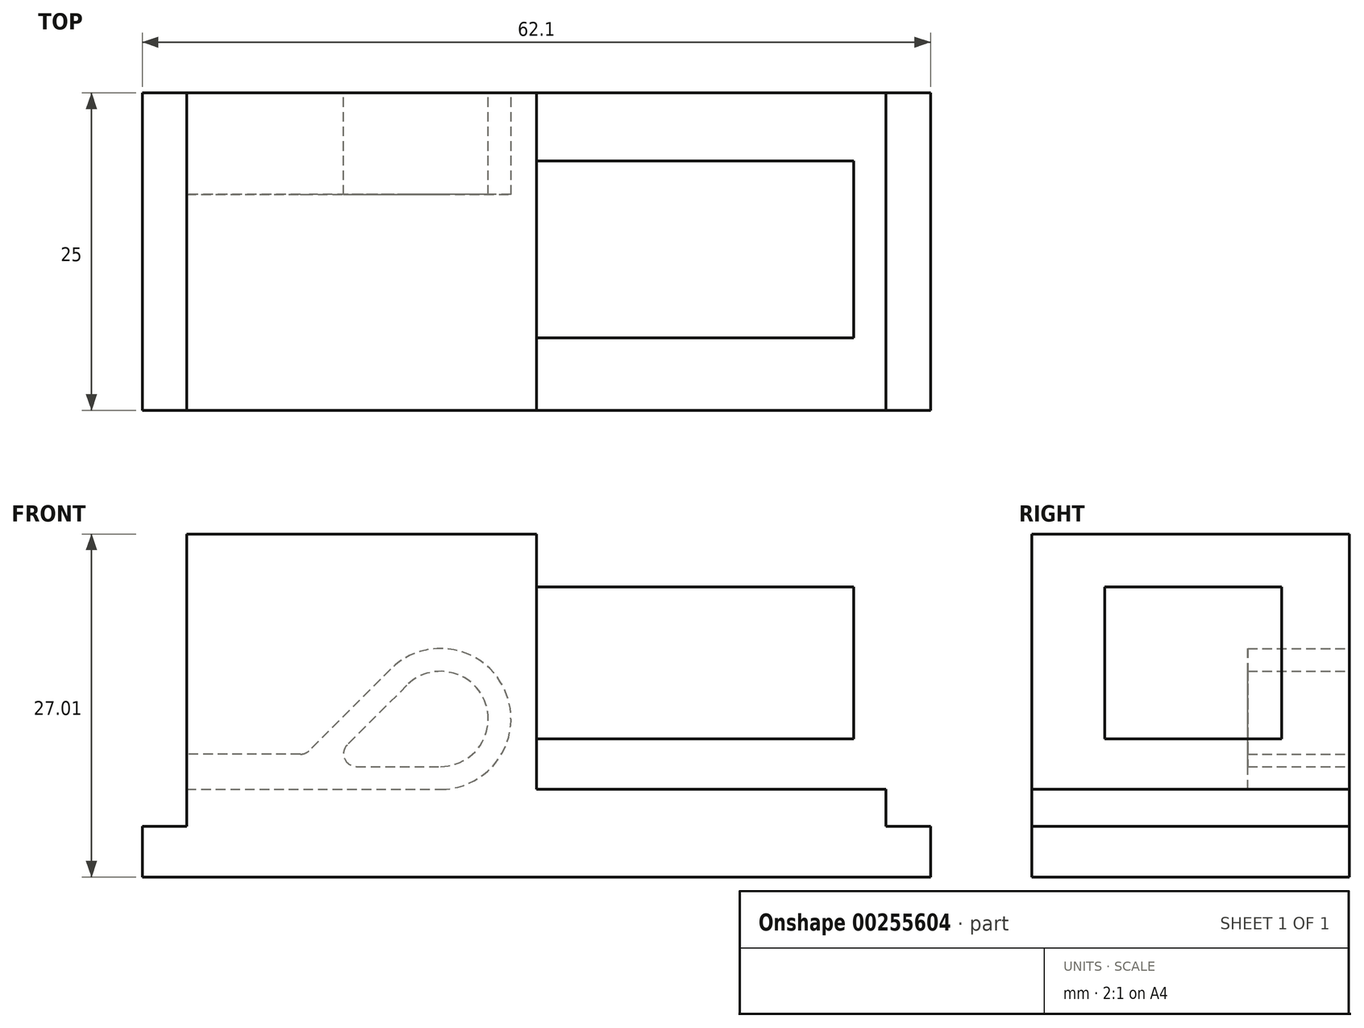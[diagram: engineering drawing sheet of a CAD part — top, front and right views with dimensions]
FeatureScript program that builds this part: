
annotation { "Feature Type Name" : "Feature", "Feature Type Description" : "" }
export const myFeature = defineFeature(function(context is Context, id is Id, definition is map)
    precondition{}
    {
        {
            var Q0;
            Q0=qCreatedBy(makeId("Front.planeOp"),FACE);
            var sketch = newSketch(context, id + "F0", { "sketchPlane" : qUnion([Q0])});
            skLineSegment(sketch, "E0.bottom", {"start": v(-31.05, 0) * mm, "end": v(31.05, 0) * mm});
            skLineSegment(sketch, "E0.top", {"start": v(-31.05, 4) * mm, "end": v(-27.55, 4) * mm});
            skLineSegment(sketch, "E0.left", {"start": v(-31.05, 0) * mm, "end": v(-31.05, 4) * mm});
            skLineSegment(sketch, "E0.right", {"start": v(31.05, 0) * mm, "end": v(31.05, 4) * mm});
            skLineSegment(sketch, "E1", {"start": v(-27.55, 4) * mm, "end": v(-27.55, 27.01) * mm});
            skLineSegment(sketch, "E2", {"start": v(-27.55, 6.9) * mm, "end": v(-7.55, 6.9) * mm});
            skLineSegment(sketch, "E3", {"start": v(27.55, 6.9) * mm, "end": v(27.55, 4) * mm});
            skLineSegment(sketch, "E4.trimOffspring", {"start": v(27.55, 4) * mm, "end": v(31.05, 4) * mm});
            skLineSegment(sketch, "E5", {"start": v(-29.3, 9.9) * mm, "end": v(-29.3, -4.78) * mm, "construction": true});
            skLineSegment(sketch, "E6", {"start": v(29.3, -4.78) * mm, "end": v(29.3, 11.42) * mm, "construction": true});
            skLineSegment(sketch, "E7.bottom", {"start": v(-27.55, 27.01) * mm, "end": v(0, 27.01) * mm});
            skLineSegment(sketch, "E7.right", {"start": v(0, 27.01) * mm, "end": v(0, 6.9) * mm});
            skLineSegment(sketch, "E8", {"start": v(-14.19, 8.7) * mm, "end": v(-7.55, 8.7) * mm});
            skArc(sketch, "E9", {"start": v(-7.55, 8.7) * mm, "mid": v(-4.09, 13.89) * mm, "end": v(-10.2, 15.1) * mm});
            skLineSegment(sketch, "E10", {"start": v(-10.2, 15.1) * mm, "end": v(-14.9, 10.4) * mm});
            skArc(sketch, "E11", {"start": v(-7.55, 6.9) * mm, "mid": v(-2.42, 14.57) * mm, "end": v(-11.47, 16.37) * mm});
            skLineSegment(sketch, "E12", {"start": v(-11.47, 16.37) * mm, "end": v(-17.89, 9.96) * mm});
            skArc(sketch, "E13.filletArc", {"start": v(-14.9, 10.4) * mm, "mid": v(-15.11, 9.32) * mm, "end": v(-14.19, 8.7) * mm});
            skLineSegment(sketch, "E14", {"start": v(-18.6, 9.67) * mm, "end": v(-27.55, 9.67) * mm});
            skPoint(sketch, "E15.visualSharp", {"position": v(-18.18, 9.67) * mm});
            skArc(sketch, "E15.filletArc", {"start": v(-18.6, 9.67) * mm, "mid": v(-18.21, 9.75) * mm, "end": v(-17.89, 9.96) * mm});
            skPoint(sketch, "E16.orphan", {"position": v(0, 3.93) * mm});
            skLineSegment(sketch, "E17.trimOffspring", {"start": v(0, 6.9) * mm, "end": v(27.55, 6.9) * mm});
            skSolve(sketch);
        }
        {
            var Q0;
            Q0=makeQuery(id+"F0.imprint","IMPRINT",FACE,{"disambiguationData":[TD([[makeQuery(id+"F0.imprint","IMPRINT",EDGE,{"derivedFrom":sQuery(id+"F0.wireOp",EDGE,"E0.bottom")}),1.0]])]});
            var Q1;
            {var subQ0=sQuery(id+"F0.wireOp",EDGE,"E2");Q1=makeQuery(id+"F0.imprint","IMPRINT",FACE,{"disambiguationData":[TD([[makeQuery(id+"F0.imprint","IMPRINT",EDGE,{"derivedFrom":subQ0}),1.0]])]});}
            var Q2;
            Q2=makeQuery(id+"F0.imprint","IMPRINT",FACE,{"disambiguationData":[TD([[makeQuery(id+"F0.imprint","IMPRINT",EDGE,{"derivedFrom":sQuery(id+"F0.wireOp",EDGE,"E8")}),1.0]])]});
            extrude(context, id + "F1", {"entities" : qUnion([Q0, Q1, Q2]), "depth" : 25 * mm});
        }
        {
            var Q0;
            {var subQ0=sQuery(id+"F0.wireOp",EDGE,"E2");Q0=makeQuery(id+"F0.imprint","IMPRINT",FACE,{"disambiguationData":[TD([[makeQuery(id+"F0.imprint","IMPRINT",EDGE,{"derivedFrom":subQ0}),1.0]])]});}
            extrude(context, id + "F2", {"entities" : qUnion([Q0]), "operationType" : NewBodyOperationType.REMOVE, "depth" : 8 * mm});
        }
        {
            var Q0;
            Q0=makeQuery(id+"F1.opExtrude","SWEPT_FACE",FACE,{"disambiguationData":[OSD([sQuery(id+"F0.wireOp",EDGE,"E7.right")])]});
            var sketch = newSketch(context, id + "F3", { "sketchPlane" : qUnion([Q0])});
            skLineSegment(sketch, "E18.bottom", {"start": v(-19.28, 22.83) * mm, "end": v(-5.34, 22.83) * mm});
            skLineSegment(sketch, "E18.top", {"start": v(-19.28, 10.9) * mm, "end": v(-5.34, 10.9) * mm});
            skLineSegment(sketch, "E18.left", {"start": v(-19.28, 22.83) * mm, "end": v(-19.28, 10.9) * mm});
            skLineSegment(sketch, "E18.right", {"start": v(-5.34, 22.83) * mm, "end": v(-5.34, 10.9) * mm});
            skSolve(sketch);
        }
        {
            var Q0;
            Q0=makeQuery(id+"F3.imprint","IMPRINT",FACE,{"disambiguationData":[TD([[makeQuery(id+"F3.imprint","IMPRINT",EDGE,{"derivedFrom":sQuery(id+"F3.wireOp",EDGE,"E18.bottom")}),-1.0]])]});
            extrude(context, id + "F4", {"entities" : qUnion([Q0]), "operationType" : NewBodyOperationType.ADD, "depth" : 25 * mm});
        }
    });
